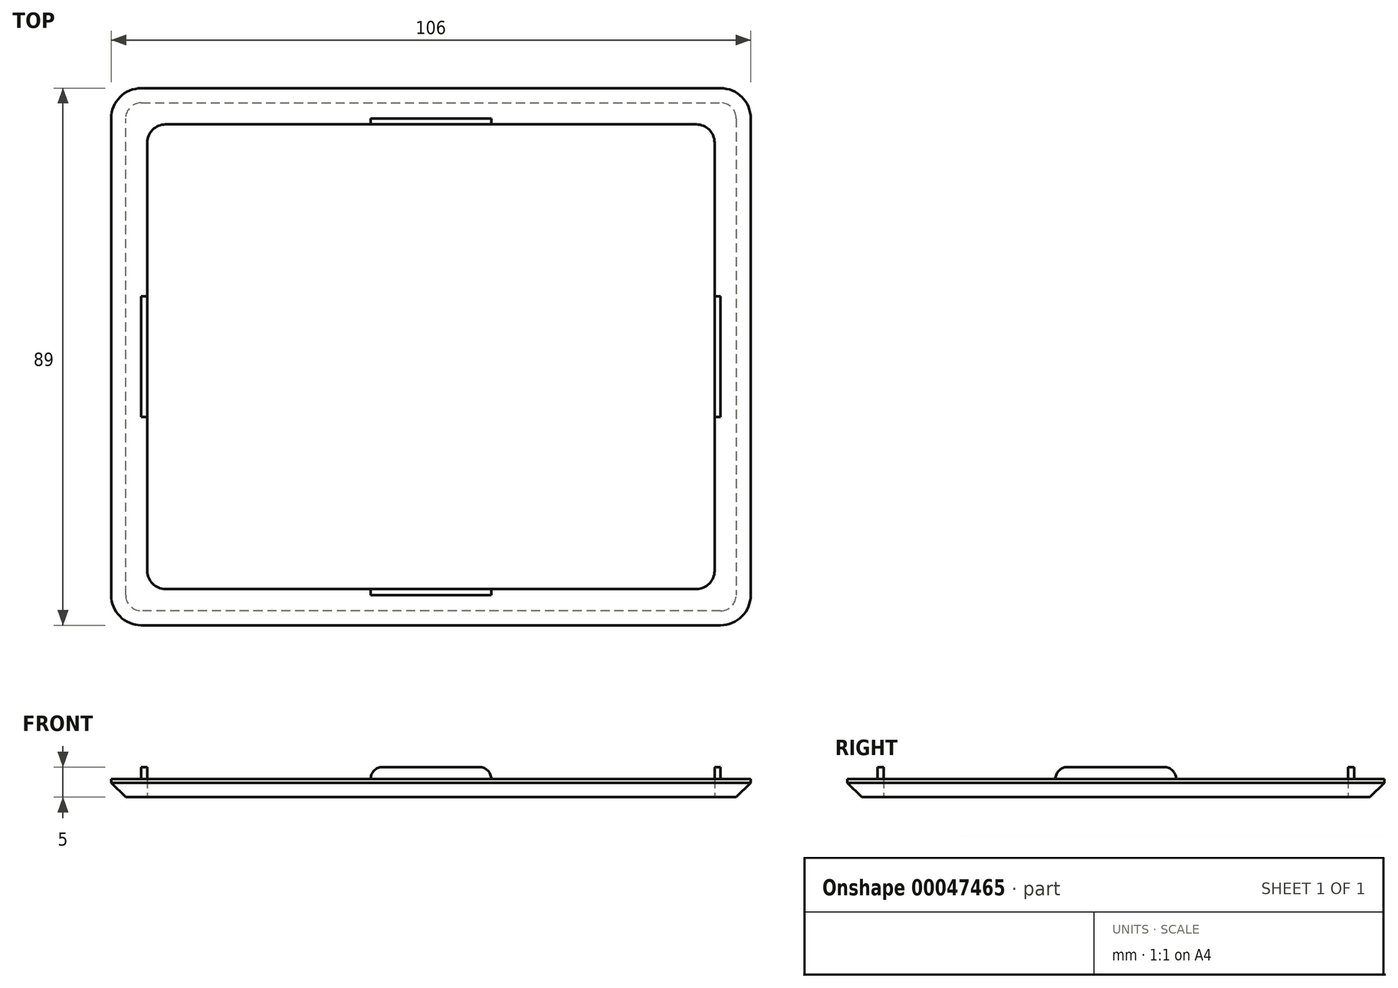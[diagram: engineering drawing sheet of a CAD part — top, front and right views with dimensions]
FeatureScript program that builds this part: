
annotation { "Feature Type Name" : "Feature", "Feature Type Description" : "" }
export const myFeature = defineFeature(function(context is Context, id is Id, definition is map)
    precondition{}
    {
        {
            var Q0;
            Q0=qCreatedBy(makeId("Top.planeOp"),FACE);
            var sketch = newSketch(context, id + "F0", { "sketchPlane" : qUnion([Q0])});
            skLineSegment(sketch, "E0.bottom", {"start": v(-47, 38.5) * mm, "end": v(47, 38.5) * mm});
            skLineSegment(sketch, "E0.top", {"start": v(-47, -38.5) * mm, "end": v(47, -38.5) * mm});
            skLineSegment(sketch, "E0.left", {"start": v(-47, 38.5) * mm, "end": v(-47, -38.5) * mm});
            skLineSegment(sketch, "E0.right", {"start": v(47, 38.5) * mm, "end": v(47, -38.5) * mm});
            skLineSegment(sketch, "E1", {"start": v(-58.32, 0) * mm, "end": v(67.05, 0) * mm, "construction": true});
            skLineSegment(sketch, "E2", {"start": v(0, 50.6) * mm, "end": v(0, -54.5) * mm, "construction": true});
            skLineSegment(sketch, "E3.0", {"start": v(-53, 44.5) * mm, "end": v(53, 44.5) * mm});
            skLineSegment(sketch, "E3.1", {"start": v(-53, 44.5) * mm, "end": v(-53, -44.5) * mm});
            skLineSegment(sketch, "E3.2", {"start": v(-53, -44.5) * mm, "end": v(53, -44.5) * mm});
            skLineSegment(sketch, "E3.3", {"start": v(53, 44.5) * mm, "end": v(53, -44.5) * mm});
            skLineSegment(sketch, "E4", {"start": v(-47, 10) * mm, "end": v(-48, 10) * mm});
            skLineSegment(sketch, "E5", {"start": v(-48, 10) * mm, "end": v(-48, -10) * mm});
            skLineSegment(sketch, "E6", {"start": v(-48, -10) * mm, "end": v(-47, -10) * mm});
            skLineSegment(sketch, "E7.MirrorCS", {"start": v(47, 10) * mm, "end": v(48, 10) * mm});
            skLineSegment(sketch, "E8.MirrorCS", {"start": v(48, 10) * mm, "end": v(48, -10) * mm});
            skLineSegment(sketch, "E9.MirrorCS", {"start": v(48, -10) * mm, "end": v(47, -10) * mm});
            skPoint(sketch, "E10", {"position": v(-53, 0) * mm});
            skLineSegment(sketch, "E11", {"start": v(-10, -38.5) * mm, "end": v(-10, -39.5) * mm});
            skLineSegment(sketch, "E12", {"start": v(-10, -39.5) * mm, "end": v(10, -39.5) * mm});
            skLineSegment(sketch, "E13", {"start": v(10, -39.5) * mm, "end": v(10, -38.5) * mm});
            skLineSegment(sketch, "E14.MirrorCS", {"start": v(-10, 39.5) * mm, "end": v(10, 39.5) * mm});
            skLineSegment(sketch, "E15.MirrorCS", {"start": v(-10, 38.5) * mm, "end": v(-10, 39.5) * mm});
            skLineSegment(sketch, "E16.MirrorCS", {"start": v(10, 39.5) * mm, "end": v(10, 38.5) * mm});
            skSolve(sketch);
        }
        {
            var Q0;
            Q0=makeQuery(id+"F0.imprint","IMPRINT",FACE,{"disambiguationData":[TD([[makeQuery(id+"F0.imprint","IMPRINT",EDGE,{"derivedFrom":sQuery(id+"F0.wireOp",EDGE,"E0.bottom")}),1.0]])]});
            var Q1;
            Q1=makeQuery(id+"F0.imprint","IMPRINT",FACE,{"disambiguationData":[TD([[makeQuery(id+"F0.imprint","IMPRINT",EDGE,{"derivedFrom":sQuery(id+"F0.wireOp",EDGE,"E3.0")}),-1.0]])]});
            extrude(context, id + "F1", {"entities" : qUnion([Q0, Q1]), "depth" : 1 * mm});
        }
        {
            var Q0;
            Q0=makeQuery(id+"F0.imprint","IMPRINT",FACE,{"disambiguationData":[TD([[makeQuery(id+"F0.imprint","IMPRINT",EDGE,{"derivedFrom":sQuery(id+"F0.wireOp",EDGE,"E14.MirrorCS")}),-1.0]])]});
            var Q1;
            {var subQ0=sQuery(id+"F0.wireOp",EDGE,"E4");Q1=makeQuery(id+"F0.imprint","IMPRINT",FACE,{"disambiguationData":[TD([[makeQuery(id+"F0.imprint","IMPRINT",EDGE,{"derivedFrom":subQ0}),1.0]])]});}
            var Q2;
            {var subQ0=sQuery(id+"F0.wireOp",EDGE,"E7.MirrorCS");Q2=makeQuery(id+"F0.imprint","IMPRINT",FACE,{"disambiguationData":[TD([[makeQuery(id+"F0.imprint","IMPRINT",EDGE,{"derivedFrom":subQ0}),-1.0]])]});}
            var Q3;
            {var subQ0=sQuery(id+"F0.wireOp",EDGE,"E11");Q3=makeQuery(id+"F0.imprint","IMPRINT",FACE,{"disambiguationData":[TD([[makeQuery(id+"F0.imprint","IMPRINT",EDGE,{"derivedFrom":subQ0}),1.0]])]});}
            extrude(context, id + "F2", {"entities" : qUnion([Q0, Q1, Q2, Q3]), "operationType" : NewBodyOperationType.ADD, "depth" : 3 * mm});
        }
        {
            var Q0;
            {var subQ13=sQuery(id+"F0.wireOp",EDGE,"E4");Q0=makeQuery(id+"F0.imprint","IMPRINT",FACE,{"disambiguationData":[TD([[makeQuery(id+"F0.imprint","IMPRINT",EDGE,{"derivedFrom":subQ13}),-1.0]])]});}
            var Q1;
            Q1=makeQuery(id+"F0.imprint","IMPRINT",FACE,{"disambiguationData":[TD([[makeQuery(id+"F0.imprint","IMPRINT",EDGE,{"derivedFrom":sQuery(id+"F0.wireOp",EDGE,"E14.MirrorCS")}),-1.0]])]});
            var Q2;
            {var subQ0=sQuery(id+"F0.wireOp",EDGE,"E7.MirrorCS");Q2=makeQuery(id+"F0.imprint","IMPRINT",FACE,{"disambiguationData":[TD([[makeQuery(id+"F0.imprint","IMPRINT",EDGE,{"derivedFrom":subQ0}),-1.0]])]});}
            var Q3;
            {var subQ0=sQuery(id+"F0.wireOp",EDGE,"E4");Q3=makeQuery(id+"F0.imprint","IMPRINT",FACE,{"disambiguationData":[TD([[makeQuery(id+"F0.imprint","IMPRINT",EDGE,{"derivedFrom":subQ0}),1.0]])]});}
            var Q4;
            {var subQ0=sQuery(id+"F0.wireOp",EDGE,"E11");Q4=makeQuery(id+"F0.imprint","IMPRINT",FACE,{"disambiguationData":[TD([[makeQuery(id+"F0.imprint","IMPRINT",EDGE,{"derivedFrom":subQ0}),1.0]])]});}
            extrude(context, id + "F3", {"entities" : qUnion([Q0, Q1, Q2, Q3, Q4]), "operationType" : NewBodyOperationType.ADD, "oppositeDirection" : true, "depth" : 2 * mm});
        }
        {
            var Q0;
            {var subQ0=sQuery(id+"F0.wireOp",EDGE,"E0.right");var subQ1=sQuery(id+"F0.wireOp",EDGE,"E0.bottom");Q0=makeQuery(id+"F3.boolean.opBoolean","MERGE",EDGE,{"derivedFrom":[makeQuery(id+"F1.opExtrude","SWEPT_EDGE",EDGE,{"disambiguationData":[OSD([subQ1,subQ0])]}),makeQuery(id+"F3.opExtrude","SWEPT_EDGE",EDGE,{"disambiguationData":[OSD([subQ1,subQ0])]})]});}
            var Q1;
            {var subQ0=sQuery(id+"F0.wireOp",EDGE,"E0.right");var subQ1=sQuery(id+"F0.wireOp",EDGE,"E0.top");Q1=makeQuery(id+"F3.boolean.opBoolean","MERGE",EDGE,{"derivedFrom":[makeQuery(id+"F1.opExtrude","SWEPT_EDGE",EDGE,{"disambiguationData":[OSD([subQ1,subQ0])]}),makeQuery(id+"F3.opExtrude","SWEPT_EDGE",EDGE,{"disambiguationData":[OSD([subQ1,subQ0])]})]});}
            var Q2;
            {var subQ0=sQuery(id+"F0.wireOp",EDGE,"E0.left");var subQ1=sQuery(id+"F0.wireOp",EDGE,"E0.bottom");Q2=makeQuery(id+"F3.boolean.opBoolean","MERGE",EDGE,{"derivedFrom":[makeQuery(id+"F1.opExtrude","SWEPT_EDGE",EDGE,{"disambiguationData":[OSD([subQ1,subQ0])]}),makeQuery(id+"F3.opExtrude","SWEPT_EDGE",EDGE,{"disambiguationData":[OSD([subQ1,subQ0])]})]});}
            var Q3;
            {var subQ0=sQuery(id+"F0.wireOp",EDGE,"E0.left");var subQ1=sQuery(id+"F0.wireOp",EDGE,"E0.top");Q3=makeQuery(id+"F3.boolean.opBoolean","MERGE",EDGE,{"derivedFrom":[makeQuery(id+"F1.opExtrude","SWEPT_EDGE",EDGE,{"disambiguationData":[OSD([subQ1,subQ0])]}),makeQuery(id+"F3.opExtrude","SWEPT_EDGE",EDGE,{"disambiguationData":[OSD([subQ1,subQ0])]})]});}
            fillet(context, id + "F4", {"entities" : qUnion([Q0, Q1, Q2, Q3]), "radius" : 3 * mm, "tangentPropagation" : true, "allowEdgeOverflow" : false});
        }
        {
            var Q0;
            Q0=makeQuery(id+"F3.opExtrude","SWEPT_EDGE",EDGE,{"disambiguationData":[OSD([sQuery(id+"F0.wireOp",EDGE,"E3.1"),sQuery(id+"F0.wireOp",EDGE,"E3.2")])]});
            var Q1;
            Q1=makeQuery(id+"F3.opExtrude","SWEPT_EDGE",EDGE,{"disambiguationData":[OSD([sQuery(id+"F0.wireOp",EDGE,"E3.2"),sQuery(id+"F0.wireOp",EDGE,"E3.3")])]});
            var Q2;
            Q2=makeQuery(id+"F3.opExtrude","SWEPT_EDGE",EDGE,{"disambiguationData":[OSD([sQuery(id+"F0.wireOp",EDGE,"E3.0"),sQuery(id+"F0.wireOp",EDGE,"E3.1")])]});
            var Q3;
            Q3=makeQuery(id+"F3.opExtrude","SWEPT_EDGE",EDGE,{"disambiguationData":[OSD([sQuery(id+"F0.wireOp",EDGE,"E3.0"),sQuery(id+"F0.wireOp",EDGE,"E3.3")])]});
            fillet(context, id + "F5", {"entities" : qUnion([Q0, Q1, Q2, Q3]), "radius" : 5 * mm, "allowEdgeOverflow" : false});
        }
        {
            var Q0;
            Q0=makeQuery(id+"F3.opExtrude","CAP_EDGE",EDGE,{"disambiguationData":[OSD([sQuery(id+"F0.wireOp",EDGE,"E3.2")])],"isStart":false});
            chamfer(context, id + "F6", {"entities" : qUnion([Q0]), "chamferType" : ChamferType.OFFSET_ANGLE, "width" : 2.4 * mm, "oppositeDirection" : false, "angle" : 45 * degree, "tangentPropagation" : true});
        }
        {
            var Q0;
            Q0=makeQuery(id+"F2.opExtrude","CAP_EDGE",EDGE,{"disambiguationData":[OSD([sQuery(id+"F0.wireOp",EDGE,"E13")])],"isStart":false});
            var Q1;
            Q1=makeQuery(id+"F2.opExtrude","CAP_EDGE",EDGE,{"disambiguationData":[OSD([sQuery(id+"F0.wireOp",EDGE,"E11")])],"isStart":false});
            var Q2;
            Q2=makeQuery(id+"F2.opExtrude","CAP_EDGE",EDGE,{"disambiguationData":[OSD([sQuery(id+"F0.wireOp",EDGE,"E6")])],"isStart":false});
            var Q3;
            Q3=makeQuery(id+"F2.opExtrude","CAP_EDGE",EDGE,{"disambiguationData":[OSD([sQuery(id+"F0.wireOp",EDGE,"E4")])],"isStart":false});
            var Q4;
            Q4=makeQuery(id+"F2.opExtrude","CAP_EDGE",EDGE,{"disambiguationData":[OSD([sQuery(id+"F0.wireOp",EDGE,"E15.MirrorCS")])],"isStart":false});
            var Q5;
            Q5=makeQuery(id+"F2.opExtrude","CAP_EDGE",EDGE,{"disambiguationData":[OSD([sQuery(id+"F0.wireOp",EDGE,"E16.MirrorCS")])],"isStart":false});
            var Q6;
            Q6=makeQuery(id+"F2.opExtrude","CAP_EDGE",EDGE,{"disambiguationData":[OSD([sQuery(id+"F0.wireOp",EDGE,"E7.MirrorCS")])],"isStart":false});
            var Q7;
            Q7=makeQuery(id+"F2.opExtrude","CAP_EDGE",EDGE,{"disambiguationData":[OSD([sQuery(id+"F0.wireOp",EDGE,"E9.MirrorCS")])],"isStart":false});
            fillet(context, id + "F7", {"entities" : qUnion([Q0, Q1, Q2, Q3, Q4, Q5, Q6, Q7]), "radius" : 2 * mm, "tangentPropagation" : true, "allowEdgeOverflow" : false});
        }
    });
